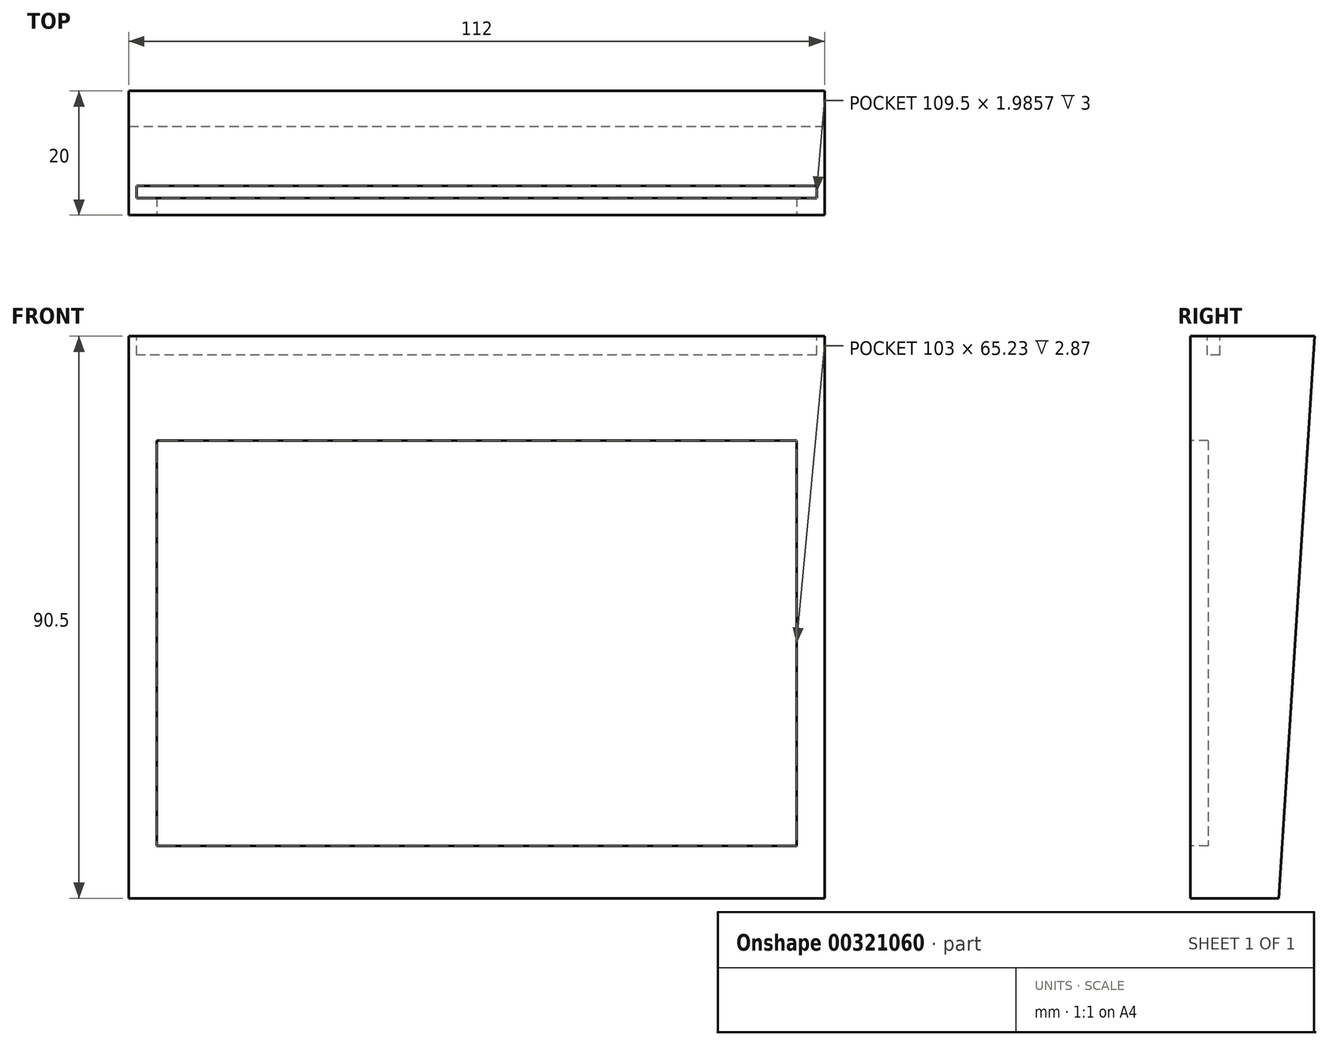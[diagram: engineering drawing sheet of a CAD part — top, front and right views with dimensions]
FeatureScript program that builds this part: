
annotation { "Feature Type Name" : "Feature", "Feature Type Description" : "" }
export const myFeature = defineFeature(function(context is Context, id is Id, definition is map)
    precondition{}
    {
        {
            var Q0;
            Q0=qCreatedBy(makeId("Front.planeOp"),FACE);
            var sketch = newSketch(context, id + "F0", { "sketchPlane" : qUnion([Q0])});
            skLineSegment(sketch, "E0.bottom", {"start": v(56, 45.25) * mm, "end": v(-56, 45.25) * mm});
            skLineSegment(sketch, "E0.top", {"start": v(56, -45.25) * mm, "end": v(-56, -45.25) * mm});
            skLineSegment(sketch, "E0.left", {"start": v(56, 45.25) * mm, "end": v(56, -45.25) * mm});
            skLineSegment(sketch, "E0.right", {"start": v(-56, 45.25) * mm, "end": v(-56, -45.25) * mm});
            skPoint(sketch, "E0.middle", {"position": v(0, 0) * mm});
            skSolve(sketch);
        }
        {
            var Q0;
            Q0=qSketchRegion(id+"F0",true);
            extrude(context, id + "F1", {"entities" : qUnion([Q0]), "depth" : 20 * mm});
        }
        {
            var Q0;
            Q0=makeQuery(id+"F1.opExtrude","SWEPT_FACE",FACE,{"disambiguationData":[OSD([sQuery(id+"F0.wireOp",EDGE,"E0.right")])]});
            var sketch = newSketch(context, id + "F2", { "sketchPlane" : qUnion([Q0])});
            skLineSegment(sketch, "E1", {"start": v(0, 45.25) * mm, "end": v(0, -45.25) * mm});
            skLineSegment(sketch, "E2", {"start": v(0, -45.25) * mm, "end": v(5.75, -45.25) * mm});
            skLineSegment(sketch, "E3", {"start": v(5.75, -45.25) * mm, "end": v(0, 45.25) * mm});
            skSolve(sketch);
        }
        {
            var Q0;
            Q0=qSketchRegion(id+"F2",true);
            extrude(context, id + "F3", {"entities" : qUnion([Q0]), "operationType" : NewBodyOperationType.REMOVE, "oppositeDirection" : true, "depth" : 200 * mm});
        }
        {
            var Q0;
            Q0=makeQuery(id+"F1.opExtrude","CAP_FACE",FACE,{"disambiguationData":[OSD([sQuery(id+"F0.wireOp",EDGE,"E0.bottom"),sQuery(id+"F0.wireOp",EDGE,"E0.top"),sQuery(id+"F0.wireOp",EDGE,"E0.left"),sQuery(id+"F0.wireOp",EDGE,"E0.right")])],"isStart":false});
            var sketch = newSketch(context, id + "F4", { "sketchPlane" : qUnion([Q0])});
            skLineSegment(sketch, "E4.bottom", {"start": v(-51.5, 28.43) * mm, "end": v(51.5, 28.43) * mm});
            skLineSegment(sketch, "E4.top", {"start": v(-51.5, -36.8) * mm, "end": v(51.5, -36.8) * mm});
            skLineSegment(sketch, "E4.left", {"start": v(-51.5, 28.43) * mm, "end": v(-51.5, -36.8) * mm});
            skLineSegment(sketch, "E4.right", {"start": v(51.5, 28.43) * mm, "end": v(51.5, -36.8) * mm});
            skSolve(sketch);
        }
        {
            var Q0;
            Q0=qSketchRegion(id+"F4",true);
            extrude(context, id + "F5", {"entities" : qUnion([Q0]), "operationType" : NewBodyOperationType.REMOVE, "oppositeDirection" : true, "depth" : 2.87 * mm});
        }
        {
            var Q0;
            Q0=makeQuery(id+"F1.opExtrude","SWEPT_FACE",FACE,{"disambiguationData":[OSD([sQuery(id+"F0.wireOp",EDGE,"E0.bottom")])]});
            var sketch = newSketch(context, id + "F6", { "sketchPlane" : qUnion([Q0])});
            skLineSegment(sketch, "E5.bottom", {"start": v(54.75, -15.26) * mm, "end": v(-54.75, -15.26) * mm});
            skLineSegment(sketch, "E5.top", {"start": v(54.75, -17.25) * mm, "end": v(-54.75, -17.25) * mm});
            skLineSegment(sketch, "E5.left", {"start": v(54.75, -15.26) * mm, "end": v(54.75, -17.25) * mm});
            skLineSegment(sketch, "E5.right", {"start": v(-54.75, -15.26) * mm, "end": v(-54.75, -17.25) * mm});
            skPoint(sketch, "E5.middle", {"position": v(0, -16.26) * mm});
            skSolve(sketch);
        }
        {
            var Q0;
            Q0=qSketchRegion(id+"F6",true);
            extrude(context, id + "F7", {"entities" : qUnion([Q0]), "operationType" : NewBodyOperationType.REMOVE, "oppositeDirection" : true, "depth" : 3 * mm});
        }
    });
